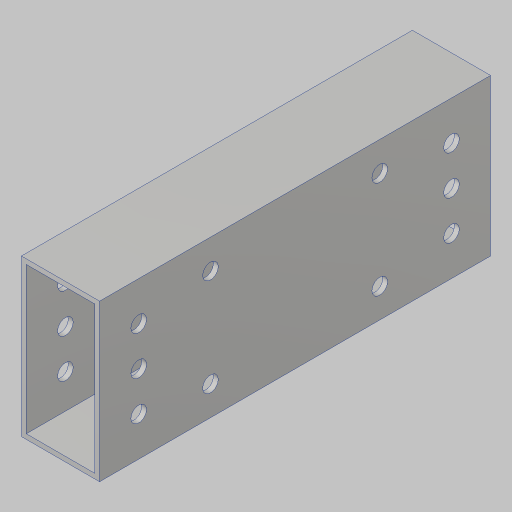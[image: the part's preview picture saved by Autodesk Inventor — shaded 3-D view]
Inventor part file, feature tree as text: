
AUTODESK INVENTOR PART (.ipt)
format: ipt  version: 2023.5 (Build 275446000, 446)  size: 141,312 bytes
history: native  units: in
note: dims shown in document units (in); Inventor stores cm internally (conversion verified against a paired STEP export)
features: extrude x1, hole x1, sketch x1
ambient origin geometry x8: Origin, YZ Plane, XZ Plane, XY Plane, X Axis, Y Axis, Z Axis, Center Point
bodies: Solid1 (feature_tree)
feature tree (3):
  extrude  "Extrusion1"  Depth=2.5in
  hole  "Hole1"  [1 undecoded]
  sketch  "Sketch2"  dims[d4=0.0in d5=2.5in d6=2.3622in d8=360.0deg d10=0.201in d11=0.75in d12=0.385in d13=0.25in d14=0.5635in d15=1.0in d16=0.8108in d17=0.5in d18=0.5in d19=0.5in]
note: 1 required parameter value undecoded (feature->parameter linkage not recoverable at this tier; creation-order binding heuristic only, values carry confidence <= 0.55)
